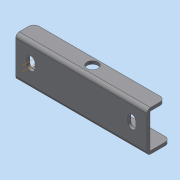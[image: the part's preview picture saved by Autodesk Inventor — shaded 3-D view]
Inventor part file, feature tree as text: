
AUTODESK INVENTOR PART (.ipt)
format: ipt  version: 2020 (Build 240168000, 168)  size: 143,872 bytes
history: native  units: mm
features: other x5, extrude x1, fillet x1
ambient origin geometry x8: Origin, YZ Plane, XZ Plane, XY Plane, X Axis, Y Axis, Z Axis, Center Point
bodies: Body1 (feature_tree)
feature tree (7):
  other  "實體1"
  extrude  "擠出1"  Depth=130.0mm
  other  "折彎零件1"
  other  "折彎零件2"
  fillet  "圓角1"  Radius=20.3mm
  other  "工作軸線2"
  other  "工作軸線3"
